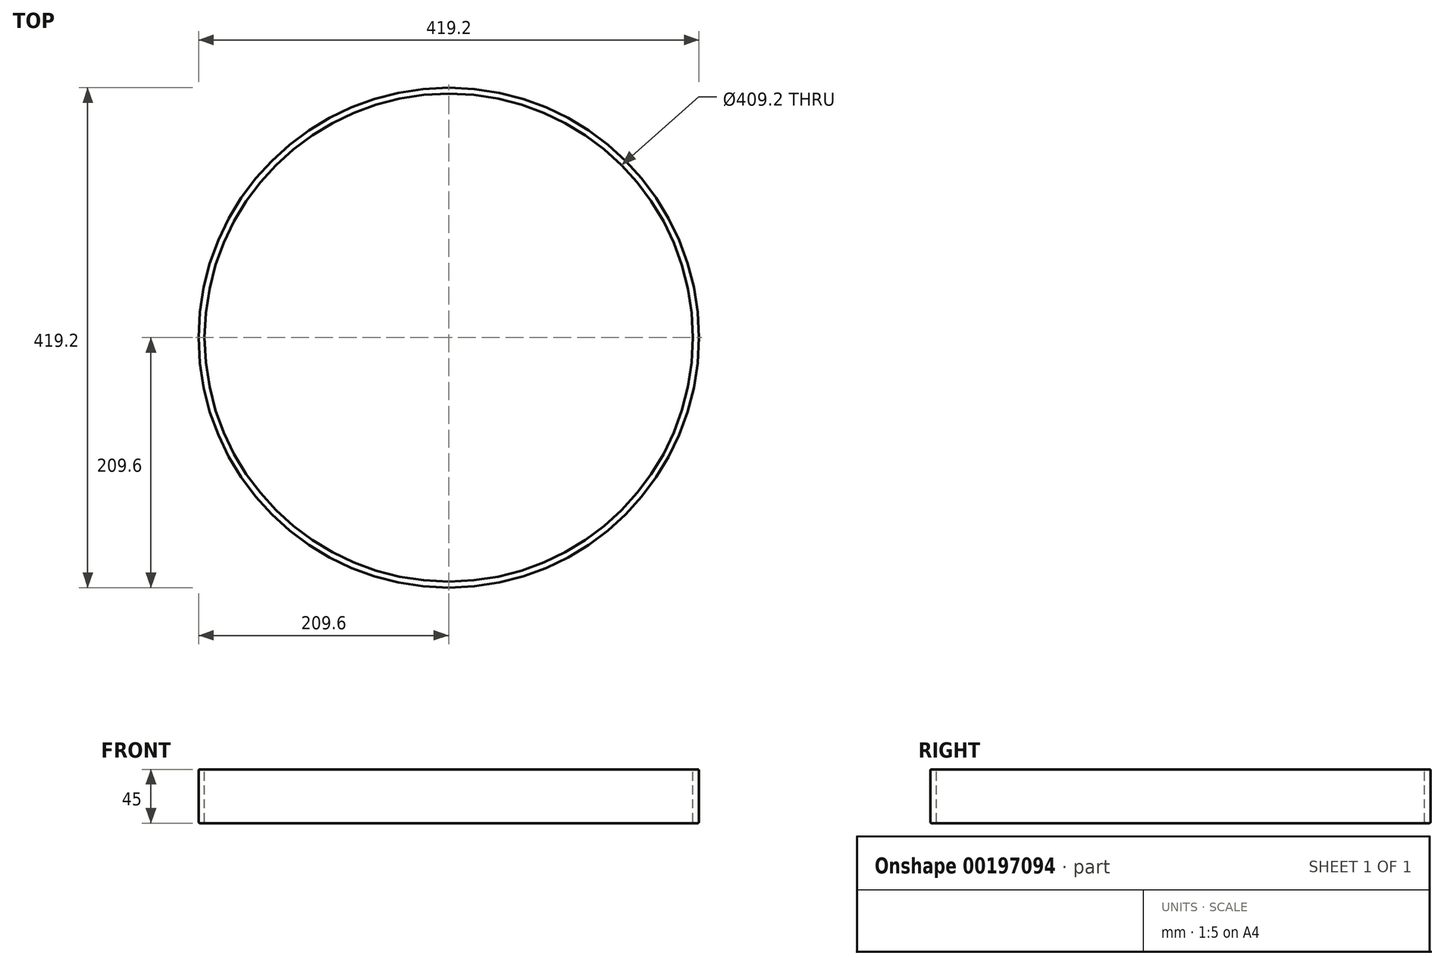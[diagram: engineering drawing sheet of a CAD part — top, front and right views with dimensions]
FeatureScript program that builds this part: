
annotation { "Feature Type Name" : "Feature", "Feature Type Description" : "" }
export const myFeature = defineFeature(function(context is Context, id is Id, definition is map)
    precondition{}
    {
        {
            var Q0;
            Q0=qCreatedBy(makeId("Front.planeOp"),FACE);
            var sketch = newSketch(context, id + "F0", { "sketchPlane" : qUnion([Q0])});
            skLineSegment(sketch, "E0", {"start": v(0, 25.64) * mm, "end": v(0, -31.1) * mm, "construction": true});
            skLineSegment(sketch, "E1", {"start": v(-208.6, 0.22) * mm, "end": v(-205.6, 0.22) * mm});
            skLineSegment(sketch, "E2", {"start": v(-204.6, -0.78) * mm, "end": v(-204.6, -43.78) * mm});
            skLineSegment(sketch, "E3", {"start": v(-209.6, -0.78) * mm, "end": v(-209.6, -43.78) * mm});
            skLineSegment(sketch, "E4", {"start": v(-208.6, -44.78) * mm, "end": v(-205.6, -44.78) * mm});
            skPoint(sketch, "E5.visualSharp", {"position": v(-204.6, 0.22) * mm});
            skArc(sketch, "E5.filletArc", {"start": v(-204.6, -0.78) * mm, "mid": v(-204.9, -0.08) * mm, "end": v(-205.6, 0.22) * mm});
            skPoint(sketch, "E6.visualSharp", {"position": v(-209.6, 0.22) * mm});
            skArc(sketch, "E6.filletArc", {"start": v(-208.6, 0.22) * mm, "mid": v(-209.3, -0.08) * mm, "end": v(-209.6, -0.78) * mm});
            skPoint(sketch, "E7.visualSharp", {"position": v(-209.6, -44.78) * mm});
            skArc(sketch, "E7.filletArc", {"start": v(-209.6, -43.78) * mm, "mid": v(-209.3, -44.5) * mm, "end": v(-208.6, -44.78) * mm});
            skPoint(sketch, "E8.visualSharp", {"position": v(-204.6, -44.78) * mm});
            skArc(sketch, "E8.filletArc", {"start": v(-205.6, -44.78) * mm, "mid": v(-204.9, -44.5) * mm, "end": v(-204.6, -43.78) * mm});
            skSolve(sketch);
        }
        {
            var Q0;
            Q0 = qSketchRegion(id + "F0", true);
            var Q1;
            Q1=sQuery(id+"F0.wireOp",EDGE,"E0");
            revolve(context, id + "F1", {"entities" : qUnion([Q0]), "axis" : qUnion([Q1]), "revolveType" : RevolveType.FULL});
        }
    });
